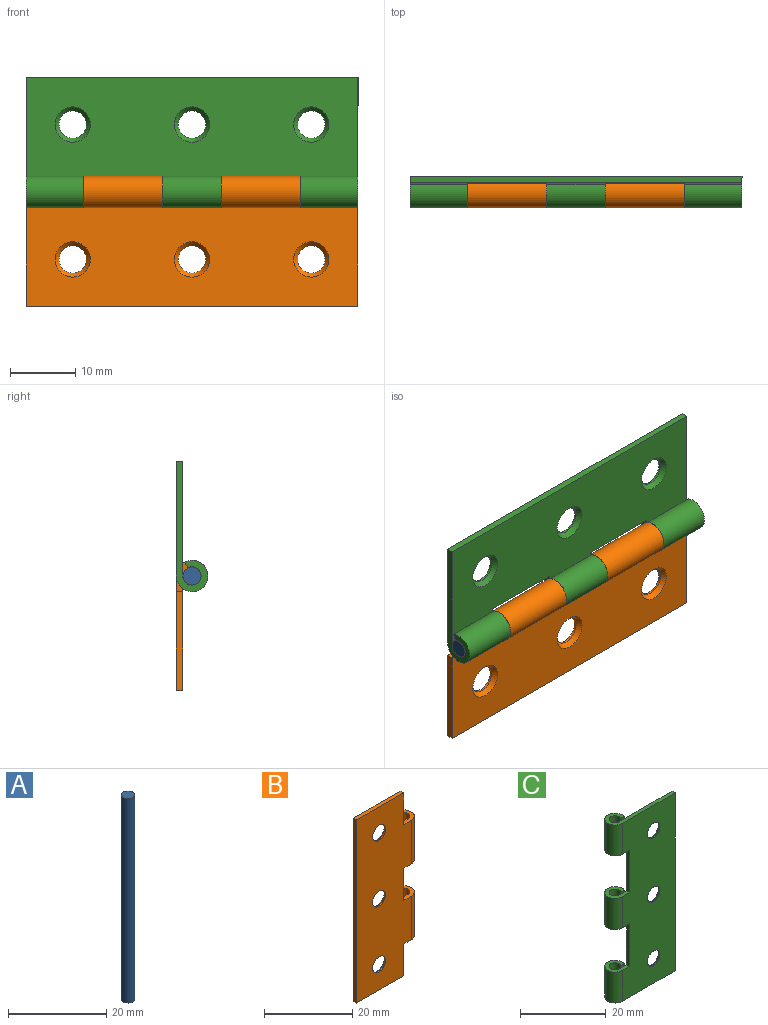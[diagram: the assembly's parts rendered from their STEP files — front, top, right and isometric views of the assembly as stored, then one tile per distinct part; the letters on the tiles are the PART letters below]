
ASSEMBLY  parts=3 mates=4
PART A: 3 faces, bbox 2.8x2.8x50.8 mm
  f0: cylinder r=1.39mm len=50.8mm, axis (0,0,1), area 442.6mm2, adj f1,f2
  f1: plane 2.77x2.77mm, normal (0,0,-1), area 6mm2, adj f0
  f2: plane 2.77x2.77mm, normal (0,0,1), area 6mm2, adj f0
PART B: 24 faces, bbox 19.9x4.8x50.8 mm
  f0: cylinder r=2.1mm len=4.19mm, axis (0,1,0), area 4.3mm2, adj f1,f12
  f1: cone r=2.69mm half-angle=41deg, axis (0,1,0), area 13.7mm2, adj f0,f14
  f2: cylinder r=2.1mm len=4.19mm, axis (0,1,0), area 4.3mm2, adj f3,f12
  f3: cone r=2.69mm half-angle=41deg, axis (0,1,0), area 13.7mm2, adj f2,f14
  f4: cylinder r=2.1mm len=4.19mm, axis (0,1,0), area 4.3mm2, adj f5,f12
  f5: cone r=2.69mm half-angle=41deg, axis (0,1,0), area 13.7mm2, adj f4,f14
  f6: cylinder r=2.41mm len=12.07mm, axis (0,0,-1), area 151mm2, adj f11,f12,f17,f21
  f7: cylinder r=1.39mm len=12.07mm, axis (0,0,-1), area 87.2mm2, adj f11,f14,f17,f21
  f8: cylinder r=2.41mm len=12.07mm, axis (0,0,-1), area 151mm2, adj f10,f12,f20,f22
  f9: cylinder r=1.39mm len=12.07mm, axis (0,0,-1), area 87.2mm2, adj f10,f14,f20,f22
  f10: plane 12.07x0.9mm, normal (0.47,-0.88,0), area 12.3mm2, adj f8,f9,f20,f22
  f11: plane 12.07x0.9mm, normal (0.47,-0.88,0), area 12.3mm2, adj f6,f7,f17,f21
  f12: plane 50.8x17.48mm, normal (0,-1,0), area 782.2mm2, adj f0,f2,f4,f6,f8,f13,f15,f16
  f13: plane 50.8x1.02mm, normal (-1,0,0), area 51.6mm2, adj f12,f14,f15,f16
  f14: plane 50.8x17.48mm, normal (0,1,0), area 755.3mm2, adj f1,f3,f5,f7,f9,f13,f15,f16
  f15: plane 15.07x1.02mm, normal (0,0,1), area 15.3mm2, adj f12,f13,f14,f23
  f16: plane 15.07x1.02mm, normal (0,0,-1), area 15.3mm2, adj f12,f13,f14,f18
  f17: plane 4.81x4.81mm, normal (0,0,-1), area 12.5mm2, adj f6,f7,f11,f12,f14,f18
  f18: plane 8.84x1.02mm, normal (1,0,0), area 9mm2, adj f12,f14,f16,f17
  f19: plane 8.99x1.02mm, normal (1,0,0), area 9.1mm2, adj f12,f14,f20,f21
  f20: plane 4.81x4.81mm, normal (0,0,-1), area 12.5mm2, adj f8,f9,f10,f12,f14,f19
  f21: plane 4.81x4.81mm, normal (0,0,1), area 12.5mm2, adj f6,f7,f11,f12,f14,f19
  f22: plane 4.81x4.81mm, normal (0,0,1), area 12.5mm2, adj f8,f9,f10,f12,f14,f23
  f23: plane 8.84x1.02mm, normal (1,0,0), area 9mm2, adj f12,f14,f15,f22
PART C: 26 faces, bbox 19.9x4.8x50.8 mm
  f0: cylinder r=2.1mm len=4.19mm, axis (0,1,0), area 4.3mm2, adj f1,f15
  f1: cone r=2.69mm half-angle=41deg, axis (0,1,0), area 13.7mm2, adj f0,f17
  f2: cylinder r=2.1mm len=4.19mm, axis (0,1,0), area 4.3mm2, adj f3,f15
  f3: cone r=2.69mm half-angle=41deg, axis (0,1,0), area 13.7mm2, adj f2,f17
  f4: cylinder r=2.1mm len=4.19mm, axis (0,1,0), area 4.3mm2, adj f5,f15
  f5: cone r=2.69mm half-angle=41deg, axis (0,1,0), area 13.7mm2, adj f4,f17
  f6: cylinder r=2.41mm len=8.79mm, axis (0,0,-1), area 110mm2, adj f14,f15,f19,f25
  f7: cylinder r=1.39mm len=8.79mm, axis (0,0,-1), area 63.5mm2, adj f14,f17,f19,f25
  f8: cylinder r=2.41mm len=8.79mm, axis (0,0,-1), area 110mm2, adj f13,f15,f18,f20
  f9: cylinder r=1.39mm len=8.79mm, axis (0,0,-1), area 63.5mm2, adj f13,f17,f18,f20
  f10: cylinder r=2.41mm len=8.89mm, axis (0,0,-1), area 111.3mm2, adj f12,f15,f22,f23
  f11: cylinder r=1.39mm len=8.89mm, axis (0,0,-1), area 64.3mm2, adj f12,f17,f22,f23
  f12: plane 8.89x0.9mm, normal (-0.47,-0.88,0), area 9mm2, adj f10,f11,f22,f23
  f13: plane 8.79x0.9mm, normal (-0.47,-0.88,0), area 8.9mm2, adj f8,f9,f18,f20
  f14: plane 8.79x0.9mm, normal (-0.47,-0.88,0), area 8.9mm2, adj f6,f7,f19,f25
  f15: plane 50.8x17.48mm, normal (0,-1,0), area 787.8mm2, adj f0,f2,f4,f6,f8,f10,f16,f18
  f16: plane 50.8x1.02mm, normal (1,0,0), area 51.6mm2, adj f15,f17,f18,f19
  f17: plane 50.8x17.48mm, normal (0,1,0), area 760.9mm2, adj f1,f3,f5,f7,f9,f11,f16,f18
  f18: plane 19.88x4.81mm, normal (0,0,1), area 27.8mm2, adj f8,f9,f13,f15,f16,f17
  f19: plane 19.88x4.81mm, normal (0,0,-1), area 27.8mm2, adj f6,f7,f14,f15,f16,f17
  f20: plane 4.81x4.81mm, normal (0,0,-1), area 12.5mm2, adj f8,f9,f13,f15,f17,f21
  f21: plane 12.17x1.02mm, normal (-1,0,0), area 12.4mm2, adj f15,f17,f20,f22
  f22: plane 4.81x4.81mm, normal (0,0,1), area 12.5mm2, adj f10,f11,f12,f15,f17,f21
  f23: plane 4.81x4.81mm, normal (0,0,-1), area 12.5mm2, adj f10,f11,f12,f15,f17,f24
  f24: plane 12.17x1.02mm, normal (-1,0,0), area 12.4mm2, adj f15,f17,f23,f25
  f25: plane 4.81x4.81mm, normal (0,0,1), area 12.5mm2, adj f6,f7,f14,f15,f17,f24
PLACE A rot(axis=(0.71,0,0.71),180deg) t=(25.4,-2.41,17.48)mm
PLACE B rot(axis=(0.71,0,0.71),180deg) t=(25.4,-2.41,17.48)mm
PLACE C rot(axis=(0.71,0,0.71),180deg) t=(25.4,-2.41,17.48)mm
MATE planar A.f0 <-> C.f18  axis (1,0,0) through (50.8,-2.41,17.48)mm
MATE cylindrical A.f0 <-> B.f6  axis (1,0,0) through (25.4,-2.41,17.48)mm
MATE planar B.f15 <-> C.f18  axis (1,0,0) through (50.8,-0.51,7.54)mm
MATE cylindrical A.f0 <-> C.f6  axis (1,0,0) through (25.4,-2.41,17.48)mm
